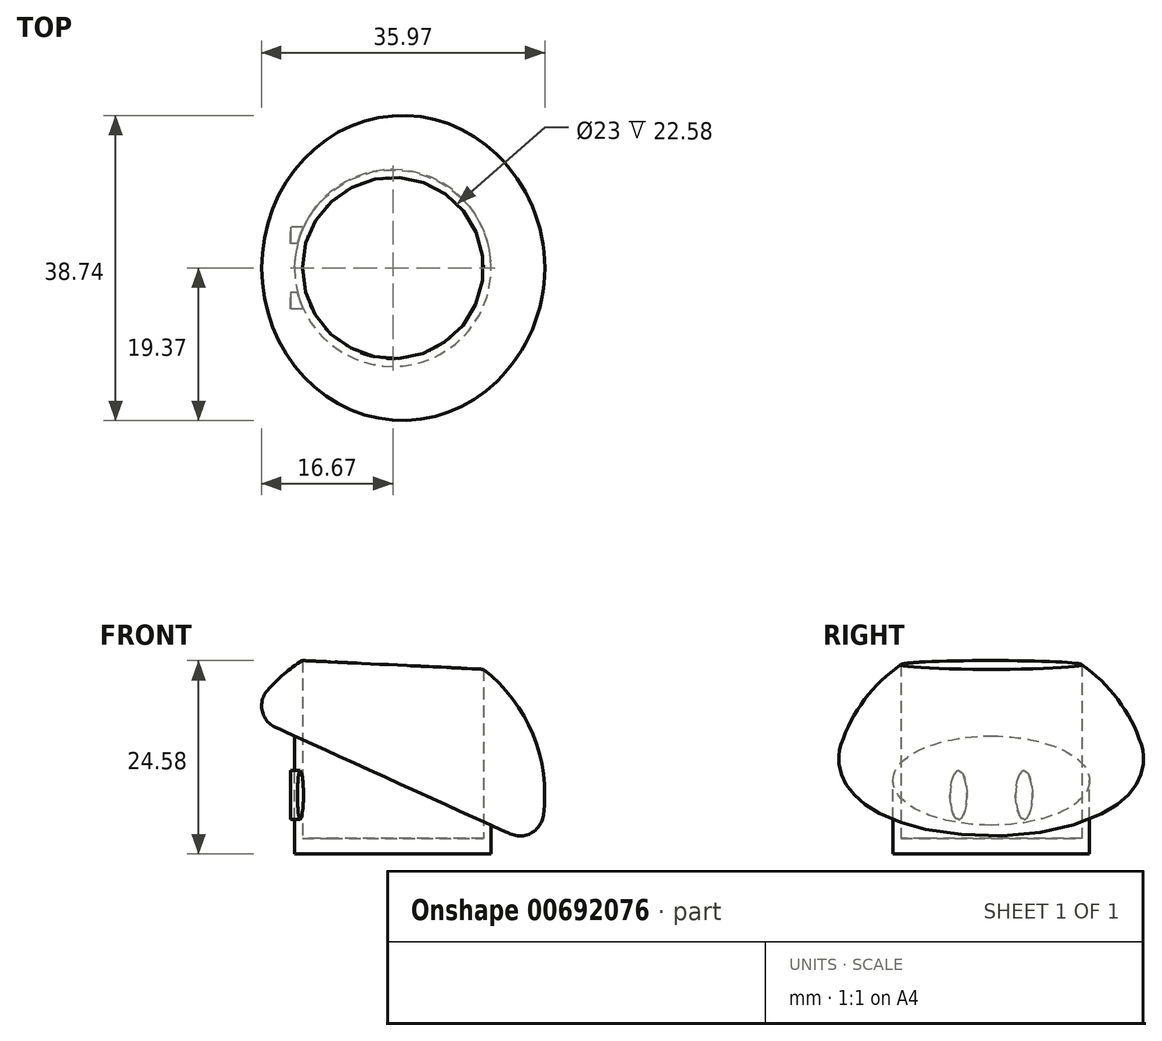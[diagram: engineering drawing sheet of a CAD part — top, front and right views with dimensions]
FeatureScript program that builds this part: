
annotation { "Feature Type Name" : "Feature", "Feature Type Description" : "" }
export const myFeature = defineFeature(function(context is Context, id is Id, definition is map)
    precondition{}
    {
        {
            var Q0;
            Q0=qCreatedBy(makeId("Top.planeOp"),FACE);
            var sketch = newSketch(context, id + "F0", { "sketchPlane" : qUnion([Q0])});
            skCircle(sketch, "E0", {"center": v(0, 0) * mm, "radius": 12.5 * mm});
            skSolve(sketch);
        }
        {
            var Q0;
            Q0 = qSketchRegion(id + "F0", true);
            extrude(context, id + "F1", {"entities" : qUnion([Q0]), "oppositeDirection" : true, "depth" : 15 * mm, "offsetDistance" : 25 * mm});
        }
        {
            var Q0;
            Q0=qCreatedBy(makeId("Front.planeOp"),FACE);
            var sketch = newSketch(context, id + "F2", { "sketchPlane" : qUnion([Q0])});
            skLineSegment(sketch, "E1", {"start": v(-12.5, -15) * mm, "end": v(-12.5, 0) * mm, "construction": true});
            skLineSegment(sketch, "E2", {"start": v(12.5, 0) * mm, "end": v(12.5, -15) * mm, "construction": true});
            skLineSegment(sketch, "E3", {"start": v(-12.5, 0) * mm, "end": v(12.5, -11.34) * mm});
            skLineSegment(sketch, "E4", {"start": v(12.5, -11.34) * mm, "end": v(12.5, 0) * mm});
            skLineSegment(sketch, "E5", {"start": v(-12.5, 0) * mm, "end": v(12.5, 0) * mm});
            skSolve(sketch);
        }
        {
            var Q0;
            Q0 = qSketchRegion(id + "F2", true);
            extrude(context, id + "F3", {"entities" : qUnion([Q0]), "operationType" : NewBodyOperationType.REMOVE, "endBound" : BoundingType.SYMMETRIC, "oppositeDirection" : true, "depth" : 30 * mm, "offsetDistance" : 25 * mm});
        }
        {
            var Q0;
            Q0=qCreatedBy(makeId("Right.planeOp"),FACE);
            var sketch = newSketch(context, id + "F4", { "sketchPlane" : qUnion([Q0])});
            skLineSegment(sketch, "E6", {"start": v(0, 0) * mm, "end": v(0, -19.1) * mm, "construction": true});
            skEllipse(sketch, "E7", {"center": v(4.16, -7.51) * mm, "majorRadius": 3.11 * mm, "minorRadius": 1.06 * mm, "majorAxis": v(0, 1)});
            skEllipse(sketch, "E8.MirrorC", {"center": v(-4.16, -7.51) * mm, "majorRadius": 3.11 * mm, "minorRadius": 1.06 * mm, "majorAxis": v(0, 1)});
            skSolve(sketch);
        }
        {
            var Q0;
            Q0 = qSketchRegion(id + "F4", true);
            extrude(context, id + "F5", {"entities" : qUnion([Q0]), "operationType" : NewBodyOperationType.ADD, "oppositeDirection" : true, "depth" : 13 * mm, "offsetDistance" : 25 * mm});
        }
        {
            var Q0;
            Q0=qCreatedBy(makeId("Front.planeOp"),FACE);
            var sketch = newSketch(context, id + "F6", { "sketchPlane" : qUnion([Q0])});
            skLineSegment(sketch, "E9.0", {"start": v(12.5, -11.34) * mm, "end": v(-12.5, 0) * mm, "construction": true});
            skSolve(sketch);
        }
        {
            var Q0;
            Q0=qCreatedBy(makeId("Front.planeOp"),FACE);
            var sketch = newSketch(context, id + "F7", { "sketchPlane" : qUnion([Q0])});
            skLineSegment(sketch, "E10", {"start": v(0, 0) * mm, "end": v(0, -21.77) * mm, "construction": true});
            skLineSegment(sketch, "E11", {"start": v(0, -4.4) * mm, "end": v(0, -4.4) * mm});
            skLineSegment(sketch, "E12.0", {"start": v(12.5, -11.34) * mm, "end": v(-12.5, 0) * mm, "construction": true});
            skPoint(sketch, "E13", {"position": v(0, -5.67) * mm});
            skLineSegment(sketch, "E14", {"start": v(0, -5.67) * mm, "end": v(18.21, -13.94) * mm});
            skLineSegment(sketch, "E15", {"start": v(0, -5.67) * mm, "end": v(-18.21, 2.6) * mm});
            skArc(sketch, "E16", {"start": v(18.21, -13.94) * mm, "mid": v(7.5, 10.87) * mm, "end": v(-18.21, 2.6) * mm});
            skLineSegment(sketch, "E17", {"start": v(0, -5.67) * mm, "end": v(7.5, 10.87) * mm, "construction": true});
            skSolve(sketch);
        }
        {
            var Q0;
            Q0=qCreatedBy(makeId("Front.planeOp"),FACE);
            var sketch = newSketch(context, id + "F8", { "sketchPlane" : qUnion([Q0])});
            skArc(sketch, "E18.0", {"start": v(18.21, -13.94) * mm, "mid": v(7.5, 10.87) * mm, "end": v(-18.21, 2.6) * mm});
            skLineSegment(sketch, "E19.0", {"start": v(0, -5.67) * mm, "end": v(18.21, -13.94) * mm});
            skLineSegment(sketch, "E20.0", {"start": v(0, -5.67) * mm, "end": v(7.5, 10.87) * mm});
            skLineSegment(sketch, "E21", {"start": v(7.5, 10.87) * mm, "end": v(0, -5.67) * mm});
            skSolve(sketch);
        }
        {
            var Q0;
            Q0 = qSketchRegion(id + "F8", true);
            var Q1;
            Q1=sQuery(id+"F8.wireOp",EDGE,"E20.0");
            revolve(context, id + "F9", {"operationType" : NewBodyOperationType.ADD, "entities" : qUnion([Q0]), "axis" : qUnion([Q1]), "revolveType" : RevolveType.FULL});
        }
        {
            var Q0;
            Q0=makeQuery(id+"F9.opRevolve","SWEPT_EDGE",EDGE,{"disambiguationData":[OSD([sQuery(id+"F8.wireOp",EDGE,"E18.0"),sQuery(id+"F8.wireOp",EDGE,"E19.0")])]});
            fillet(context, id + "F10", {"entities" : qUnion([Q0]), "radius" : 3 * mm, "tangentPropagation" : true, "allowEdgeOverflow" : false});
        }
        {
            var Q0;
            Q0=qCreatedBy(makeId("Top.planeOp"),FACE);
            var sketch = newSketch(context, id + "F11", { "sketchPlane" : qUnion([Q0])});
            skCircle(sketch, "E22", {"center": v(0, 0) * mm, "radius": 11.5 * mm});
            skSolve(sketch);
        }
        {
            var Q0;
            Q0 = qSketchRegion(id + "F11", true);
            extrude(context, id + "F12", {"entities" : qUnion([Q0]), "operationType" : NewBodyOperationType.REMOVE, "endBound" : BoundingType.THROUGH_ALL, "depth" : 13 * mm, "offsetDistance" : 25 * mm});
        }
        {
            var Q0;
            Q0=makeQuery(id+"F12.boolean.opBoolean","COPY",FACE,{"derivedFrom":makeQuery(id+"F12.opExtrude","CAP_FACE",FACE,{"disambiguationData":[OSD([sQuery(id+"F11.wireOp",EDGE,"E22")])],"isStart":true})});
            var sketch = newSketch(context, id + "F13", { "sketchPlane" : qUnion([Q0])});
            skCircle(sketch, "E23.0", {"center": v(0, 0) * mm, "radius": 11.5 * mm});
            skSolve(sketch);
        }
        {
            var Q0;
            Q0=makeQuery(id+"F13.imprint","IMPRINT",FACE,{"disambiguationData":[TD([[makeQuery(id+"F13.imprint","IMPRINT",EDGE,{"derivedFrom":sQuery(id+"F13.wireOp",EDGE,"E23.0")}),1.0]])]});
            var sketch = newSketch(context, id + "F14", { "sketchPlane" : qUnion([Q0])});
            skCircle(sketch, "E24", {"center": v(0, 0) * mm, "radius": 11.5 * mm});
            skSolve(sketch);
        }
        {
            var Q0;
            Q0 = qSketchRegion(id + "F14", true);
            extrude(context, id + "F15", {"entities" : qUnion([Q0]), "operationType" : NewBodyOperationType.REMOVE, "oppositeDirection" : true, "depth" : 13 * mm, "offsetDistance" : 25 * mm});
        }
    });
